# Revit family: Haworth_MeetingPoints_Table_Round_EU_PRELIMINARY
name_source: partatom
category: Furniture
units: mm (PartAtom-declared; Revit-internal decimal feet)

## family parameters
Always vertical = Yes
Cut with Voids When Loaded = No
OmniClass Number = 23.40.70.14.64.21
OmniClass Title = Systems Furniture
Room Calculation Point = No
Shared = No
Work Plane-Based = No

## types (7) — shared parameters
Assembly Code = E2020200
Description = Haworth - Meeting Points - Table - Round
Glide Finish = Haworth _ Polymer _ Black
Manufacturer = Haworth
Max. Diameter = 120 cm
Max. Height = 110 cm
Min. Diameter = 70 cm
Min. Height = 74 cm
Model = A00000004
Revision Number = 1
Size = Verify Final Dim. w/ Haworth
Standard Widths = 70, 80, 90, 100, 120 cm
URL = https://www.haworth.com
URL - Product = https://www.haworth.com
Warranty = http://www.haworth.com

## per-type parameters (varying)
| type | Actual Diameter | Actual Height | Base Height | Casters | Diameter | Disc Base Support | Disc Radius | Four Star Base | Glides | Height | Large | Radius | Small |
| 70cm x 74h - with Casters | 70 cm | 74 cm | 71 cm | Yes | 70 cm | No | 30 cm | Yes | No | 74 cm | No | 35 cm | Yes |
| 80cm x 110h - with Glides | 80 cm | 110 cm | 107 cm | No | 80 cm | No | 30 cm | Yes | Yes | 110 cm | No | 40 cm | Yes |
| 90cm x 74h - with Casters | 90 cm | 74 cm | 71 cm | Yes | 90 cm | No | 30 cm | Yes | No | 74 cm | No | 45 cm | Yes |
| 100cm x 110h - with Glides | 100 cm | 110 cm | 107 cm | No | 100 cm | No | 30 cm | Yes | Yes | 110 cm | No | 50 cm | Yes |
| 120cm x 74h - with Disc Base | 120 cm | 74 cm | 71 cm | No | 120 cm | Yes | 45 cm | No | No | 74 cm | Yes | 60 cm | No |
| 90cm x 74h - with Disc Base | 90 cm | 74 cm | 71 cm | No | 90 cm | Yes | 30 cm | No | No | 74 cm | No | 45 cm | Yes |
| 70cm x 110h - with Glides | 70 cm | 110 cm | 107 cm | No | 70 cm | No | 30 cm | Yes | Yes | 110 cm | No | 35 cm | Yes |

## geometry (parser evidence)
native form markers: Blend x4, Sweep x11
no freeform markers — native parametric forms only
